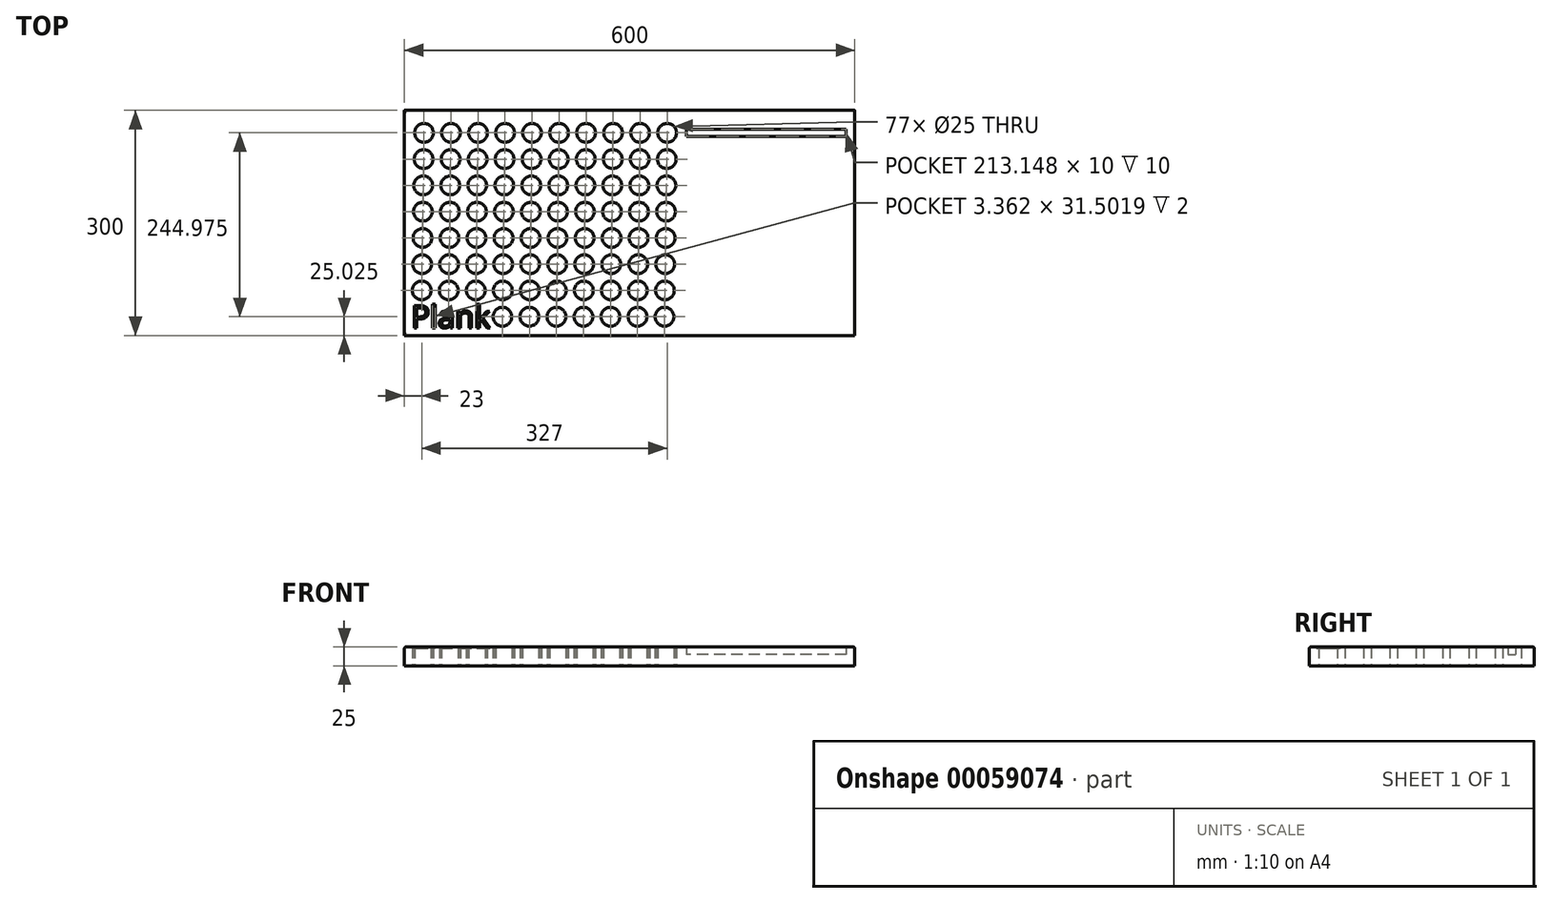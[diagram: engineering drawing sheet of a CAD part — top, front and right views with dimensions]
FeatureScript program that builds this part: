
annotation { "Feature Type Name" : "Feature", "Feature Type Description" : "" }
export const myFeature = defineFeature(function(context is Context, id is Id, definition is map)
    precondition{}
    {
        {
            var Q0;
            Q0=qCreatedBy(makeId("Top.planeOp"),FACE);
            var sketch = newSketch(context, id + "F0", { "sketchPlane" : qUnion([Q0])});
            skLineSegment(sketch, "E0.rect.bottom", {"start": v(300, -150) * mm, "end": v(-300, -150) * mm});
            skLineSegment(sketch, "E0.rect.top", {"start": v(300, 150) * mm, "end": v(-300, 150) * mm});
            skLineSegment(sketch, "E0.rect.left", {"start": v(300, -150) * mm, "end": v(300, 150) * mm});
            skLineSegment(sketch, "E0.rect.right", {"start": v(-300, -150) * mm, "end": v(-300, 150) * mm});
            skPoint(sketch, "E0.rect.middle", {"position": v(0, 0) * mm});
            skCircle(sketch, "E1", {"center": v(-274, 120) * mm, "radius": 12.5 * mm});
            skCircle(sketch, "E2.0.1.0", {"center": v(-274.5, 85) * mm, "radius": 12.5 * mm});
            skCircle(sketch, "E2.1.0.0", {"center": v(-238, 120) * mm, "radius": 12.5 * mm});
            skCircle(sketch, "E2.1.1.0", {"center": v(-238.5, 85) * mm, "radius": 12.5 * mm});
            skCircle(sketch, "E2.2.0.0", {"center": v(-202, 120) * mm, "radius": 12.5 * mm});
            skCircle(sketch, "E2.2.1.0", {"center": v(-202.5, 85) * mm, "radius": 12.5 * mm});
            skLineSegment(sketch, "E2.direction1", {"start": v(-274, 120) * mm, "end": v(-238, 120) * mm, "construction": true});
            skLineSegment(sketch, "E2.direction2", {"start": v(-274, 120) * mm, "end": v(-274.5, 85) * mm, "construction": true});
            skCircle(sketch, "E3.0.3.0", {"center": v(-166, 120) * mm, "radius": 12.5 * mm});
            skCircle(sketch, "E3.0.3.1", {"center": v(-166.5, 85) * mm, "radius": 12.5 * mm});
            skCircle(sketch, "E3.0.4.0", {"center": v(-130, 120) * mm, "radius": 12.5 * mm});
            skCircle(sketch, "E3.0.4.1", {"center": v(-130.5, 85) * mm, "radius": 12.5 * mm});
            skCircle(sketch, "E3.0.5.0", {"center": v(-94, 120) * mm, "radius": 12.5 * mm});
            skCircle(sketch, "E3.0.5.1", {"center": v(-94.5, 85) * mm, "radius": 12.5 * mm});
            skCircle(sketch, "E3.0.6.0", {"center": v(-58, 120) * mm, "radius": 12.5 * mm});
            skCircle(sketch, "E3.0.6.1", {"center": v(-58.5, 85) * mm, "radius": 12.5 * mm});
            skCircle(sketch, "E3.0.7.0", {"center": v(-22, 120) * mm, "radius": 12.5 * mm});
            skCircle(sketch, "E3.0.7.1", {"center": v(-22.5, 85) * mm, "radius": 12.5 * mm});
            skCircle(sketch, "E3.0.8.0", {"center": v(14, 120) * mm, "radius": 12.5 * mm});
            skCircle(sketch, "E3.0.8.1", {"center": v(13.5, 85) * mm, "radius": 12.5 * mm});
            skCircle(sketch, "E3.0.9.0", {"center": v(50, 120) * mm, "radius": 12.5 * mm});
            skCircle(sketch, "E3.0.9.1", {"center": v(49.5, 85) * mm, "radius": 12.5 * mm});
            skCircle(sketch, "E4.0.0.2", {"center": v(-275, 50) * mm, "radius": 12.5 * mm});
            skCircle(sketch, "E4.0.0.3", {"center": v(-275.5, 15.01) * mm, "radius": 12.5 * mm});
            skCircle(sketch, "E4.0.0.4", {"center": v(-276, -19.99) * mm, "radius": 12.5 * mm});
            skCircle(sketch, "E4.0.0.5", {"center": v(-276.5, -54.98) * mm, "radius": 12.5 * mm});
            skCircle(sketch, "E4.0.1.2", {"center": v(-239, 50) * mm, "radius": 12.5 * mm});
            skCircle(sketch, "E4.0.1.3", {"center": v(-239.5, 15.01) * mm, "radius": 12.5 * mm});
            skCircle(sketch, "E4.0.1.4", {"center": v(-240, -19.99) * mm, "radius": 12.5 * mm});
            skCircle(sketch, "E4.0.1.5", {"center": v(-240.5, -54.98) * mm, "radius": 12.5 * mm});
            skCircle(sketch, "E4.0.2.2", {"center": v(-203, 50) * mm, "radius": 12.5 * mm});
            skCircle(sketch, "E4.0.2.3", {"center": v(-203.5, 15.01) * mm, "radius": 12.5 * mm});
            skCircle(sketch, "E4.0.2.4", {"center": v(-204, -19.99) * mm, "radius": 12.5 * mm});
            skCircle(sketch, "E4.0.2.5", {"center": v(-204.5, -54.98) * mm, "radius": 12.5 * mm});
            skCircle(sketch, "E4.0.3.2", {"center": v(-167, 50) * mm, "radius": 12.5 * mm});
            skCircle(sketch, "E4.0.3.3", {"center": v(-167.5, 15.01) * mm, "radius": 12.5 * mm});
            skCircle(sketch, "E4.0.3.4", {"center": v(-168, -19.99) * mm, "radius": 12.5 * mm});
            skCircle(sketch, "E4.0.3.5", {"center": v(-168.5, -54.98) * mm, "radius": 12.5 * mm});
            skCircle(sketch, "E4.0.4.2", {"center": v(-131, 50) * mm, "radius": 12.5 * mm});
            skCircle(sketch, "E4.0.4.3", {"center": v(-131.5, 15.01) * mm, "radius": 12.5 * mm});
            skCircle(sketch, "E4.0.4.4", {"center": v(-132, -19.99) * mm, "radius": 12.5 * mm});
            skCircle(sketch, "E4.0.4.5", {"center": v(-132.5, -54.98) * mm, "radius": 12.5 * mm});
            skCircle(sketch, "E4.0.5.2", {"center": v(-95, 50) * mm, "radius": 12.5 * mm});
            skCircle(sketch, "E4.0.5.3", {"center": v(-95.5, 15.01) * mm, "radius": 12.5 * mm});
            skCircle(sketch, "E4.0.5.4", {"center": v(-96, -19.99) * mm, "radius": 12.5 * mm});
            skCircle(sketch, "E4.0.5.5", {"center": v(-96.5, -54.98) * mm, "radius": 12.5 * mm});
            skCircle(sketch, "E4.0.6.2", {"center": v(-59, 50) * mm, "radius": 12.5 * mm});
            skCircle(sketch, "E4.0.6.3", {"center": v(-59.5, 15.01) * mm, "radius": 12.5 * mm});
            skCircle(sketch, "E4.0.6.4", {"center": v(-60, -19.99) * mm, "radius": 12.5 * mm});
            skCircle(sketch, "E4.0.6.5", {"center": v(-60.5, -54.98) * mm, "radius": 12.5 * mm});
            skCircle(sketch, "E4.0.7.2", {"center": v(-23, 50) * mm, "radius": 12.5 * mm});
            skCircle(sketch, "E4.0.7.3", {"center": v(-23.5, 15.01) * mm, "radius": 12.5 * mm});
            skCircle(sketch, "E4.0.7.4", {"center": v(-24, -19.99) * mm, "radius": 12.5 * mm});
            skCircle(sketch, "E4.0.7.5", {"center": v(-24.5, -54.98) * mm, "radius": 12.5 * mm});
            skCircle(sketch, "E4.0.8.2", {"center": v(13, 50) * mm, "radius": 12.5 * mm});
            skCircle(sketch, "E4.0.8.3", {"center": v(12.5, 15.01) * mm, "radius": 12.5 * mm});
            skCircle(sketch, "E4.0.8.4", {"center": v(12, -19.99) * mm, "radius": 12.5 * mm});
            skCircle(sketch, "E4.0.8.5", {"center": v(11.5, -54.98) * mm, "radius": 12.5 * mm});
            skCircle(sketch, "E4.0.9.2", {"center": v(49, 50) * mm, "radius": 12.5 * mm});
            skCircle(sketch, "E4.0.9.3", {"center": v(48.5, 15.01) * mm, "radius": 12.5 * mm});
            skCircle(sketch, "E4.0.9.4", {"center": v(48, -19.99) * mm, "radius": 12.5 * mm});
            skCircle(sketch, "E4.0.9.5", {"center": v(47.5, -54.98) * mm, "radius": 12.5 * mm});
            skCircle(sketch, "E5.0.0.6", {"center": v(-277, -89.98) * mm, "radius": 12.5 * mm});
            skCircle(sketch, "E5.0.1.6", {"center": v(-241, -89.98) * mm, "radius": 12.5 * mm});
            skCircle(sketch, "E5.0.2.6", {"center": v(-205, -89.98) * mm, "radius": 12.5 * mm});
            skCircle(sketch, "E5.0.3.6", {"center": v(-169, -89.98) * mm, "radius": 12.5 * mm});
            skCircle(sketch, "E5.0.3.7", {"center": v(-169.5, -124.97) * mm, "radius": 12.5 * mm});
            skCircle(sketch, "E5.0.4.6", {"center": v(-133, -89.98) * mm, "radius": 12.5 * mm});
            skCircle(sketch, "E5.0.4.7", {"center": v(-133.5, -124.97) * mm, "radius": 12.5 * mm});
            skCircle(sketch, "E5.0.5.6", {"center": v(-97, -89.98) * mm, "radius": 12.5 * mm});
            skCircle(sketch, "E5.0.5.7", {"center": v(-97.5, -124.97) * mm, "radius": 12.5 * mm});
            skCircle(sketch, "E5.0.6.6", {"center": v(-61, -89.98) * mm, "radius": 12.5 * mm});
            skCircle(sketch, "E5.0.6.7", {"center": v(-61.5, -124.97) * mm, "radius": 12.5 * mm});
            skCircle(sketch, "E5.0.7.6", {"center": v(-25, -89.98) * mm, "radius": 12.5 * mm});
            skCircle(sketch, "E5.0.7.7", {"center": v(-25.5, -124.97) * mm, "radius": 12.5 * mm});
            skCircle(sketch, "E5.0.8.6", {"center": v(11, -89.98) * mm, "radius": 12.5 * mm});
            skCircle(sketch, "E5.0.8.7", {"center": v(10.5, -124.97) * mm, "radius": 12.5 * mm});
            skCircle(sketch, "E5.0.9.6", {"center": v(47, -89.98) * mm, "radius": 12.5 * mm});
            skCircle(sketch, "E5.0.9.7", {"center": v(46.5, -124.97) * mm, "radius": 12.5 * mm});
            skLineSegment(sketch, "E6.rect.bottom", {"start": v(288.57, 115) * mm, "end": v(75.43, 115) * mm});
            skLineSegment(sketch, "E6.rect.top", {"start": v(288.57, 125) * mm, "end": v(75.43, 125) * mm});
            skLineSegment(sketch, "E6.rect.left", {"start": v(288.57, 115) * mm, "end": v(288.57, 125) * mm});
            skLineSegment(sketch, "E6.rect.right", {"start": v(75.43, 115) * mm, "end": v(75.43, 125) * mm});
            skPoint(sketch, "E6.rect.middle", {"position": v(182, 120) * mm});
            skSolve(sketch);
        }
        {
            var Q0;
            Q0 = qSketchRegion(id + "F0", true);
            extrude(context, id + "F1", {"entities" : qUnion([Q0]), "depth" : 25 * mm});
        }
        {
            var Q0;
            Q0=makeQuery(id+"F0.imprint","IMPRINT",FACE,{"disambiguationData":[TD([[makeQuery(id+"F0.imprint","IMPRINT",EDGE,{"derivedFrom":sQuery(id+"F0.wireOp",EDGE,"E6.rect.bottom")}),-1.0]])]});
            extrude(context, id + "F2", {"entities" : qUnion([Q0]), "operationType" : NewBodyOperationType.ADD, "depth" : 15 * mm});
        }
        {
            var Q0;
            Q0=makeQuery(id+"F1.opExtrude","CAP_EDGE",EDGE,{"disambiguationData":[OSD([sQuery(id+"F0.wireOp",EDGE,"E0.rect.top")])],"isStart":false});
            var Q1;
            Q1=makeQuery(id+"F1.opExtrude","CAP_EDGE",EDGE,{"disambiguationData":[OSD([sQuery(id+"F0.wireOp",EDGE,"E0.rect.right")])],"isStart":false});
            var Q2;
            Q2=makeQuery(id+"F1.opExtrude","CAP_EDGE",EDGE,{"disambiguationData":[OSD([sQuery(id+"F0.wireOp",EDGE,"E0.rect.bottom")])],"isStart":false});
            var Q3;
            Q3=makeQuery(id+"F1.opExtrude","CAP_EDGE",EDGE,{"disambiguationData":[OSD([sQuery(id+"F0.wireOp",EDGE,"E0.rect.left")])],"isStart":false});
            fillet(context, id + "F3", {"entities" : qUnion([Q0, Q1, Q2, Q3]), "radius" : 2 * mm, "tangentPropagation" : true, "allowEdgeOverflow" : false});
        }
        {
            var Q0;
            Q0=makeQuery(id+"F1.opExtrude","CAP_FACE",FACE,{"disambiguationData":[OSD([sQuery(id+"F0.wireOp",EDGE,"E0.rect.bottom"),sQuery(id+"F0.wireOp",EDGE,"E0.rect.top"),sQuery(id+"F0.wireOp",EDGE,"E0.rect.left"),sQuery(id+"F0.wireOp",EDGE,"E0.rect.right"),sQuery(id+"F0.wireOp",EDGE,"E1"),sQuery(id+"F0.wireOp",EDGE,"E2.0.1.0"),sQuery(id+"F0.wireOp",EDGE,"E2.1.0.0"),sQuery(id+"F0.wireOp",EDGE,"E2.1.1.0"),sQuery(id+"F0.wireOp",EDGE,"E2.2.0.0"),sQuery(id+"F0.wireOp",EDGE,"E2.2.1.0"),sQuery(id+"F0.wireOp",EDGE,"E3.0.3.0"),sQuery(id+"F0.wireOp",EDGE,"E3.0.3.1"),sQuery(id+"F0.wireOp",EDGE,"E3.0.4.0"),sQuery(id+"F0.wireOp",EDGE,"E3.0.4.1"),sQuery(id+"F0.wireOp",EDGE,"E3.0.5.0"),sQuery(id+"F0.wireOp",EDGE,"E3.0.5.1"),sQuery(id+"F0.wireOp",EDGE,"E3.0.6.0"),sQuery(id+"F0.wireOp",EDGE,"E3.0.6.1"),sQuery(id+"F0.wireOp",EDGE,"E3.0.7.0"),sQuery(id+"F0.wireOp",EDGE,"E3.0.7.1"),sQuery(id+"F0.wireOp",EDGE,"E3.0.8.0"),sQuery(id+"F0.wireOp",EDGE,"E3.0.8.1"),sQuery(id+"F0.wireOp",EDGE,"E3.0.9.0"),sQuery(id+"F0.wireOp",EDGE,"E3.0.9.1"),sQuery(id+"F0.wireOp",EDGE,"E4.0.0.2"),sQuery(id+"F0.wireOp",EDGE,"E4.0.0.3"),sQuery(id+"F0.wireOp",EDGE,"E4.0.0.4"),sQuery(id+"F0.wireOp",EDGE,"E4.0.0.5"),sQuery(id+"F0.wireOp",EDGE,"E4.0.1.2"),sQuery(id+"F0.wireOp",EDGE,"E4.0.1.3"),sQuery(id+"F0.wireOp",EDGE,"E4.0.1.4"),sQuery(id+"F0.wireOp",EDGE,"E4.0.1.5"),sQuery(id+"F0.wireOp",EDGE,"E4.0.2.2"),sQuery(id+"F0.wireOp",EDGE,"E4.0.2.3"),sQuery(id+"F0.wireOp",EDGE,"E4.0.2.4"),sQuery(id+"F0.wireOp",EDGE,"E4.0.2.5"),sQuery(id+"F0.wireOp",EDGE,"E4.0.3.2"),sQuery(id+"F0.wireOp",EDGE,"E4.0.3.3"),sQuery(id+"F0.wireOp",EDGE,"E4.0.3.4"),sQuery(id+"F0.wireOp",EDGE,"E4.0.3.5"),sQuery(id+"F0.wireOp",EDGE,"E4.0.4.2"),sQuery(id+"F0.wireOp",EDGE,"E4.0.4.3"),sQuery(id+"F0.wireOp",EDGE,"E4.0.4.4"),sQuery(id+"F0.wireOp",EDGE,"E4.0.4.5"),sQuery(id+"F0.wireOp",EDGE,"E4.0.5.2"),sQuery(id+"F0.wireOp",EDGE,"E4.0.5.3"),sQuery(id+"F0.wireOp",EDGE,"E4.0.5.4"),sQuery(id+"F0.wireOp",EDGE,"E4.0.5.5"),sQuery(id+"F0.wireOp",EDGE,"E4.0.6.2"),sQuery(id+"F0.wireOp",EDGE,"E4.0.6.3"),sQuery(id+"F0.wireOp",EDGE,"E4.0.6.4"),sQuery(id+"F0.wireOp",EDGE,"E4.0.6.5"),sQuery(id+"F0.wireOp",EDGE,"E4.0.7.2"),sQuery(id+"F0.wireOp",EDGE,"E4.0.7.3"),sQuery(id+"F0.wireOp",EDGE,"E4.0.7.4"),sQuery(id+"F0.wireOp",EDGE,"E4.0.7.5"),sQuery(id+"F0.wireOp",EDGE,"E4.0.8.2"),sQuery(id+"F0.wireOp",EDGE,"E4.0.8.3"),sQuery(id+"F0.wireOp",EDGE,"E4.0.8.4"),sQuery(id+"F0.wireOp",EDGE,"E4.0.8.5"),sQuery(id+"F0.wireOp",EDGE,"E4.0.9.2"),sQuery(id+"F0.wireOp",EDGE,"E4.0.9.3"),sQuery(id+"F0.wireOp",EDGE,"E4.0.9.4"),sQuery(id+"F0.wireOp",EDGE,"E4.0.9.5"),sQuery(id+"F0.wireOp",EDGE,"E5.0.0.6"),sQuery(id+"F0.wireOp",EDGE,"E5.0.1.6"),sQuery(id+"F0.wireOp",EDGE,"E5.0.2.6"),sQuery(id+"F0.wireOp",EDGE,"E5.0.3.6"),sQuery(id+"F0.wireOp",EDGE,"E5.0.3.7"),sQuery(id+"F0.wireOp",EDGE,"E5.0.4.6"),sQuery(id+"F0.wireOp",EDGE,"E5.0.4.7"),sQuery(id+"F0.wireOp",EDGE,"E5.0.5.6"),sQuery(id+"F0.wireOp",EDGE,"E5.0.5.7"),sQuery(id+"F0.wireOp",EDGE,"E5.0.6.6"),sQuery(id+"F0.wireOp",EDGE,"E5.0.6.7"),sQuery(id+"F0.wireOp",EDGE,"E5.0.7.6"),sQuery(id+"F0.wireOp",EDGE,"E5.0.7.7"),sQuery(id+"F0.wireOp",EDGE,"E5.0.8.6"),sQuery(id+"F0.wireOp",EDGE,"E5.0.8.7"),sQuery(id+"F0.wireOp",EDGE,"E5.0.9.6"),sQuery(id+"F0.wireOp",EDGE,"E5.0.9.7"),sQuery(id+"F0.wireOp",EDGE,"E6.rect.bottom"),sQuery(id+"F0.wireOp",EDGE,"E6.rect.top"),sQuery(id+"F0.wireOp",EDGE,"E6.rect.left"),sQuery(id+"F0.wireOp",EDGE,"E6.rect.right")])],"isStart":false});
            var sketch = newSketch(context, id + "F4", { "sketchPlane" : qUnion([Q0])});
            skText(sketch, "E7", { "text": "Plank", "fontName": "OpenSans-Regular.ttf"});
            const initialGuessF4  = {"E7": [-0.29105, -0.13976, 1, 0, 0.02985]};
            skSetInitialGuess(sketch, initialGuessF4);
            skSolve(sketch);
        }
        {
            var Q0;
            Q0 = qSketchRegion(id + "F4", true);
            extrude(context, id + "F5", {"entities" : qUnion([Q0]), "operationType" : NewBodyOperationType.REMOVE, "oppositeDirection" : true, "depth" : 2 * mm});
        }
    });
